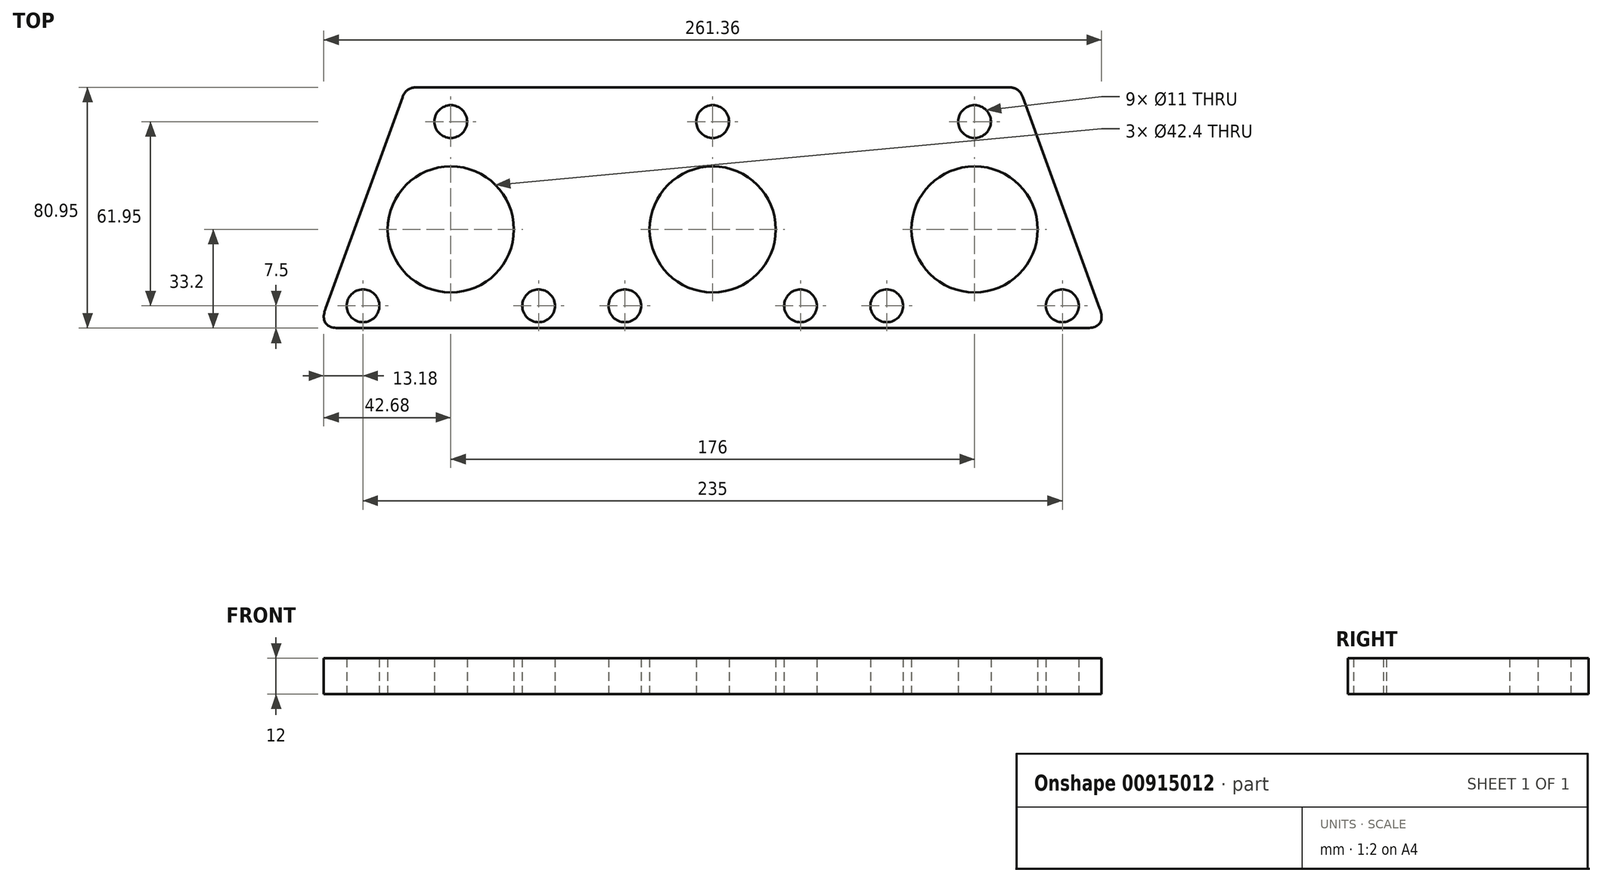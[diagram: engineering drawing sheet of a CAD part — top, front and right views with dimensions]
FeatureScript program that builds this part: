
annotation { "Feature Type Name" : "Feature", "Feature Type Description" : "" }
export const myFeature = defineFeature(function(context is Context, id is Id, definition is map)
    precondition{}
    {
        {
            var Q0;
            Q0=qCreatedBy(makeId("Top.planeOp"),FACE);
            var sketch = newSketch(context, id + "F0", { "sketchPlane" : qUnion([Q0])});
            skCircle(sketch, "E0", {"center": v(0, 0) * mm, "radius": 21.2 * mm});
            skLineSegment(sketch, "E1", {"start": v(0, 73.14) * mm, "end": v(0, -77.41) * mm, "construction": true});
            skCircle(sketch, "E2", {"center": v(-88, 0) * mm, "radius": 21.2 * mm});
            skCircle(sketch, "E3", {"center": v(88, 0) * mm, "radius": 21.2 * mm});
            skLineSegment(sketch, "E4", {"start": v(-88, -21.2) * mm, "end": v(-88, -33.2) * mm, "construction": true});
            skCircle(sketch, "E5", {"center": v(-29.5, -25.7) * mm, "radius": 5.5 * mm});
            skLineSegment(sketch, "E6", {"start": v(-29.5, -25.7) * mm, "end": v(0, -25.7) * mm, "construction": true});
            skCircle(sketch, "E7", {"center": v(29.5, -25.7) * mm, "radius": 5.5 * mm});
            skCircle(sketch, "E8", {"center": v(58.5, -25.7) * mm, "radius": 5.5 * mm});
            skLineSegment(sketch, "E9", {"start": v(29.5, -25.7) * mm, "end": v(58.5, -25.7) * mm, "construction": true});
            skLineSegment(sketch, "E10", {"start": v(58.5, -25.7) * mm, "end": v(58.5, -33.2) * mm, "construction": true});
            skCircle(sketch, "E11", {"center": v(117.5, -25.7) * mm, "radius": 5.5 * mm});
            skLineSegment(sketch, "E12", {"start": v(58.5, -25.7) * mm, "end": v(117.5, -25.7) * mm, "construction": true});
            skLineSegment(sketch, "E13", {"start": v(117.5, -25.7) * mm, "end": v(117.5, -33.2) * mm, "construction": true});
            skLineSegment(sketch, "E14.MirrorCS", {"start": v(-58.5, -25.7) * mm, "end": v(-117.5, -25.7) * mm, "construction": true});
            skLineSegment(sketch, "E15.MirrorCS", {"start": v(-29.5, -25.7) * mm, "end": v(-58.5, -25.7) * mm, "construction": true});
            skCircle(sketch, "E16.MirrorC", {"center": v(-117.5, -25.7) * mm, "radius": 5.5 * mm});
            skCircle(sketch, "E17.MirrorC", {"center": v(-58.5, -25.7) * mm, "radius": 5.5 * mm});
            skCircle(sketch, "E18", {"center": v(0, 36.25) * mm, "radius": 5.5 * mm});
            skLineSegment(sketch, "E19", {"start": v(0, 36.25) * mm, "end": v(0, 0) * mm, "construction": true});
            skCircle(sketch, "E20", {"center": v(88, 36.25) * mm, "radius": 5.5 * mm});
            skLineSegment(sketch, "E21", {"start": v(88, 36.25) * mm, "end": v(88, 0) * mm, "construction": true});
            skCircle(sketch, "E22.MirrorC", {"center": v(-88, 36.25) * mm, "radius": 5.5 * mm});
            skLineSegment(sketch, "E23", {"start": v(-103.04, 47.75) * mm, "end": v(103.04, 47.75) * mm});
            skLineSegment(sketch, "E24", {"start": v(-88, 47.75) * mm, "end": v(-88, 36.25) * mm, "construction": true});
            skLineSegment(sketch, "E25", {"start": v(-103.04, 47.75) * mm, "end": v(-132.5, -33.2) * mm});
            skLineSegment(sketch, "E26", {"start": v(103.04, 47.75) * mm, "end": v(132.5, -33.2) * mm});
            skLineSegment(sketch, "E27", {"start": v(0, -33.2) * mm, "end": v(132.5, -33.2) * mm});
            skLineSegment(sketch, "E28.MirrorCS", {"start": v(0, -139.54) * mm, "end": v(0, 11.01) * mm, "construction": true});
            skLineSegment(sketch, "E29.MirrorCS", {"start": v(0, -137.1) * mm, "end": v(0, 13.46) * mm, "construction": true});
            skLineSegment(sketch, "E30.MirrorCS", {"start": v(0, -33.2) * mm, "end": v(-132.5, -33.2) * mm});
            skLineSegment(sketch, "E31", {"start": v(-29.5, -25.7) * mm, "end": v(-29.5, -33.2) * mm, "construction": true});
            skLineSegment(sketch, "E32", {"start": v(-58.5, -25.7) * mm, "end": v(-58.5, -33.2) * mm, "construction": true});
            skLineSegment(sketch, "E33", {"start": v(-117.5, -25.7) * mm, "end": v(-117.5, -33.2) * mm, "construction": true});
            skLineSegment(sketch, "E34", {"start": v(-88, 0) * mm, "end": v(0, 0) * mm, "construction": true});
            skLineSegment(sketch, "E35", {"start": v(0, 0) * mm, "end": v(88, 0) * mm, "construction": true});
            skSolve(sketch);
        }
        {
            var Q0;
            Q0=makeQuery(id+"F0.imprint","IMPRINT",FACE,{"disambiguationData":[TD([[makeQuery(id+"F0.imprint","IMPRINT",EDGE,{"derivedFrom":sQuery(id+"F0.wireOp",EDGE,"E0")}),-1.0]])]});
            extrude(context, id + "F1", {"entities" : qUnion([Q0]), "endBound" : BoundingType.SYMMETRIC, "depth" : 12 * mm, "offsetDistance" : 25 * mm});
        }
        {
            var Q0;
            Q0=makeQuery(id+"F1.opExtrude","SWEPT_EDGE",EDGE,{"disambiguationData":[OSD([sQuery(id+"F0.wireOp",EDGE,"E25"),sQuery(id+"F0.wireOp",EDGE,"E30.MirrorCS")])]});
            var Q1;
            Q1=makeQuery(id+"F1.opExtrude","SWEPT_EDGE",EDGE,{"disambiguationData":[OSD([sQuery(id+"F0.wireOp",EDGE,"E23"),sQuery(id+"F0.wireOp",EDGE,"E25")])]});
            var Q2;
            Q2=makeQuery(id+"F1.opExtrude","SWEPT_EDGE",EDGE,{"disambiguationData":[OSD([sQuery(id+"F0.wireOp",EDGE,"E23"),sQuery(id+"F0.wireOp",EDGE,"E26")])]});
            var Q3;
            Q3=makeQuery(id+"F1.opExtrude","SWEPT_EDGE",EDGE,{"disambiguationData":[OSD([sQuery(id+"F0.wireOp",EDGE,"E26"),sQuery(id+"F0.wireOp",EDGE,"E27")])]});
            fillet(context, id + "F2", {"entities" : qUnion([Q0, Q1, Q2, Q3]), "radius" : 5 * mm, "tangentPropagation" : true, "rho" : 0.5, "crossSection" : FilletCrossSection.CONIC, "allowEdgeOverflow" : false});
        }
    });
